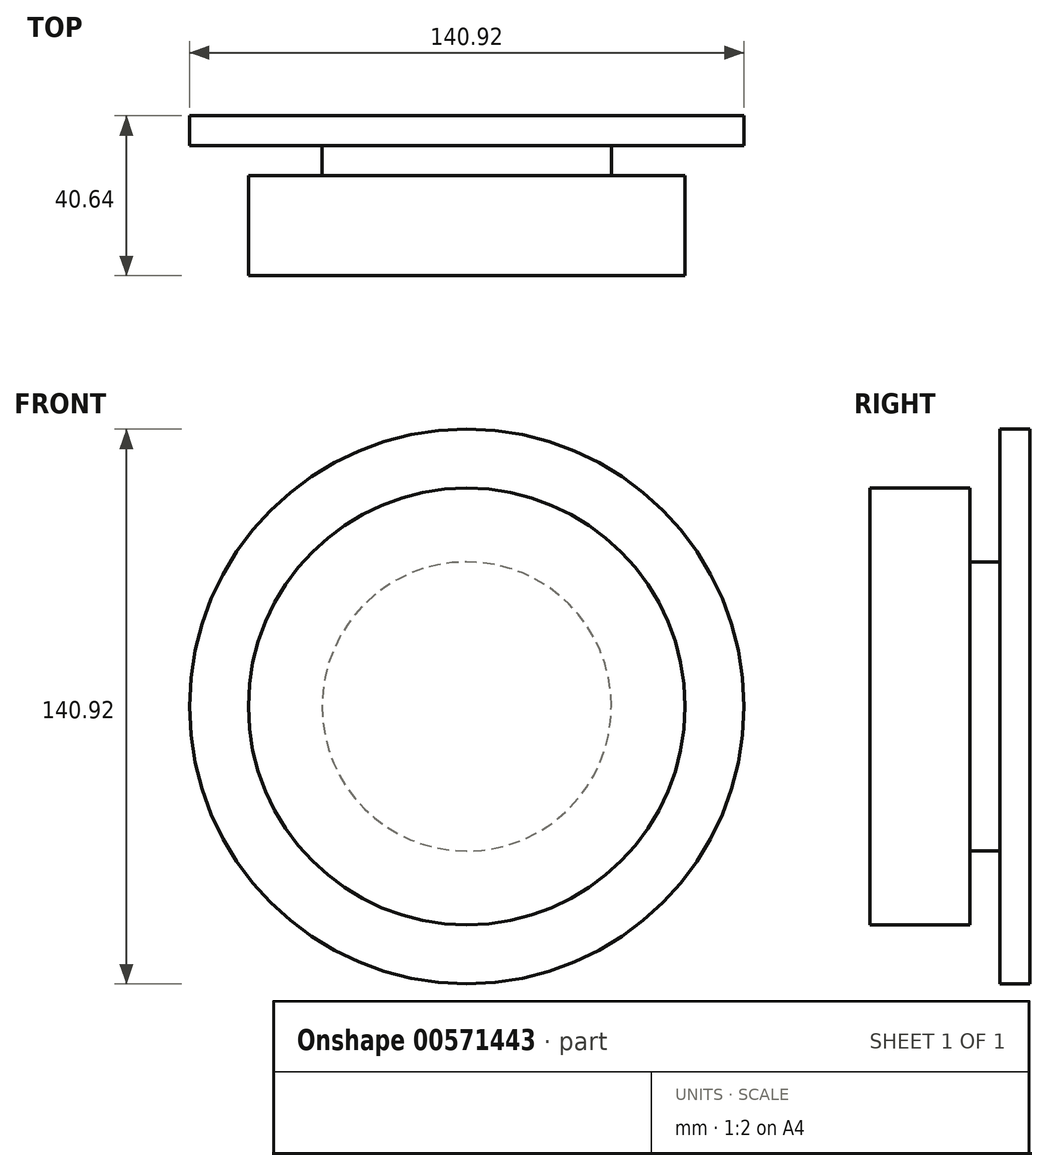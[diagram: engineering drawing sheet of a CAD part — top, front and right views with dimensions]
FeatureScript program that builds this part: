
annotation { "Feature Type Name" : "Feature", "Feature Type Description" : "" }
export const myFeature = defineFeature(function(context is Context, id is Id, definition is map)
    precondition{}
    {
        {
            var Q0;
            Q0=qCreatedBy(makeId("Front.planeOp"),FACE);
            var sketch = newSketch(context, id + "F0", { "sketchPlane" : qUnion([Q0])});
            skCircle(sketch, "E0", {"center": v(0, 0) * mm, "radius": 70.46 * mm});
            skSolve(sketch);
        }
        {
            var Q0;
            Q0=makeQuery(id+"F0.imprint","IMPRINT",FACE,{"disambiguationData":[TD([[makeQuery(id+"F0.imprint","IMPRINT",EDGE,{"derivedFrom":sQuery(id+"F0.wireOp",EDGE,"E0")}),1.0]])]});
            extrude(context, id + "F1", {"entities" : qUnion([Q0]), "depth" : 7.62 * mm, "offsetDistance" : 25.4 * mm});
        }
        {
            var Q0;
            Q0=makeQuery(id+"F1.opExtrude","CAP_FACE",FACE,{"disambiguationData":[OSD([sQuery(id+"F0.wireOp",EDGE,"E0")])],"isStart":false});
            var sketch = newSketch(context, id + "F2", { "sketchPlane" : qUnion([Q0])});
            skCircle(sketch, "E1", {"center": v(0, 0) * mm, "radius": 36.74 * mm});
            skSolve(sketch);
        }
        {
            var Q0;
            Q0 = qSketchRegion(id + "F2", true);
            extrude(context, id + "F3", {"entities" : qUnion([Q0]), "operationType" : NewBodyOperationType.ADD, "depth" : 7.62 * mm, "offsetDistance" : 25.4 * mm});
        }
        {
            var Q0;
            Q0=makeQuery(id+"F3.opExtrude","CAP_FACE",FACE,{"disambiguationData":[OSD([sQuery(id+"F2.wireOp",EDGE,"E1")])],"isStart":false});
            var sketch = newSketch(context, id + "F4", { "sketchPlane" : qUnion([Q0])});
            skCircle(sketch, "E2", {"center": v(0, 0) * mm, "radius": 55.48 * mm});
            skSolve(sketch);
        }
        {
            var Q0;
            Q0 = qSketchRegion(id + "F4", true);
            extrude(context, id + "F5", {"entities" : qUnion([Q0]), "operationType" : NewBodyOperationType.ADD, "depth" : 25.4 * mm, "offsetDistance" : 25.4 * mm});
        }
    });
